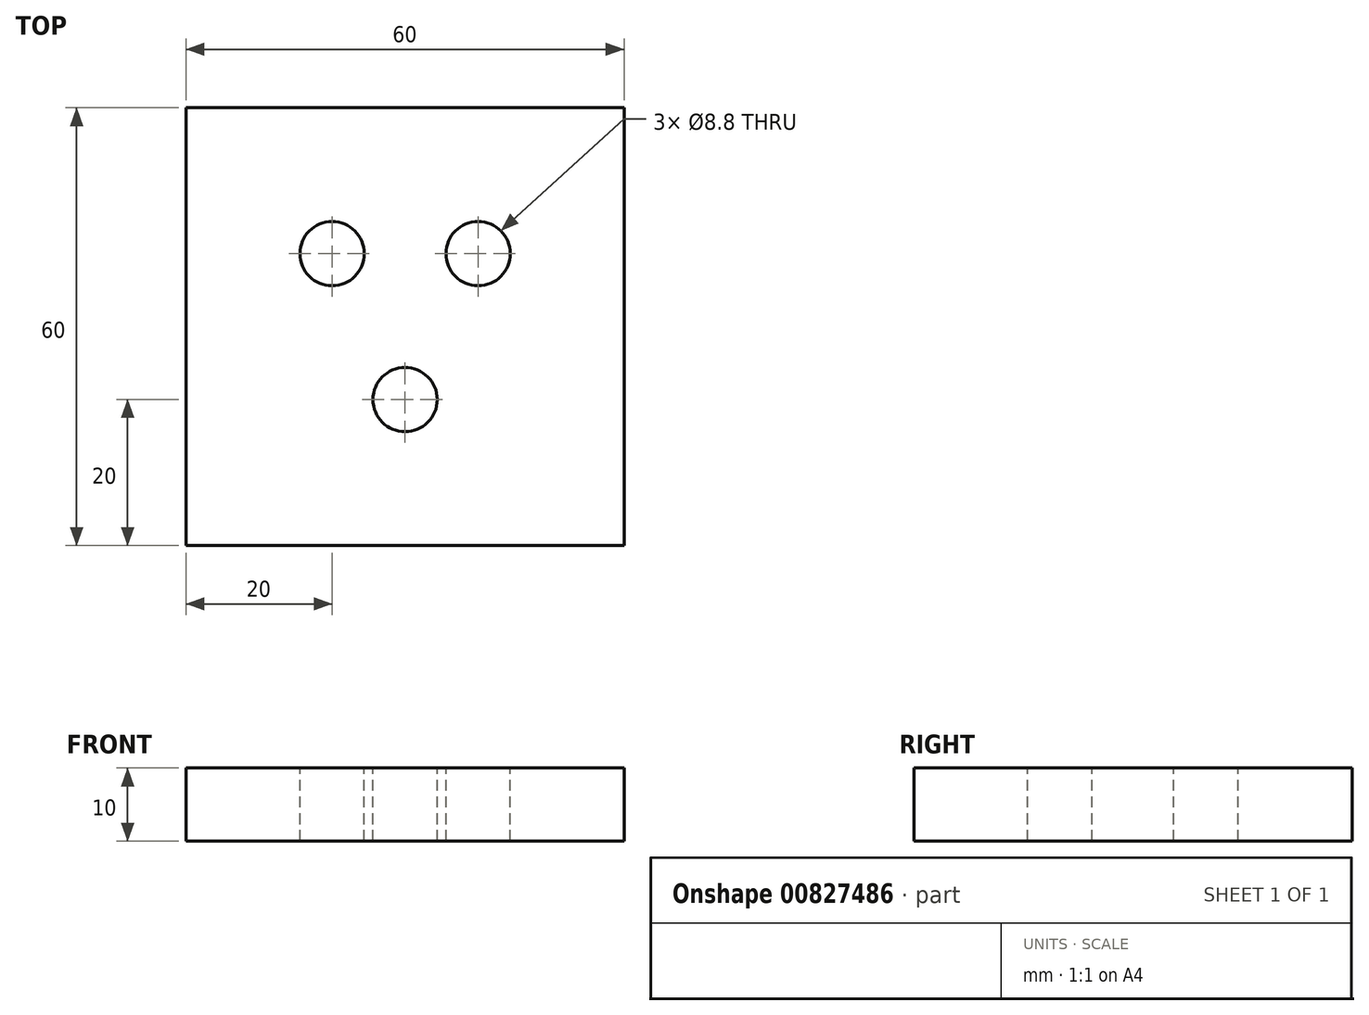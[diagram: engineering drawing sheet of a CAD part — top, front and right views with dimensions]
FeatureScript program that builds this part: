
annotation { "Feature Type Name" : "Feature", "Feature Type Description" : "" }
export const myFeature = defineFeature(function(context is Context, id is Id, definition is map)
    precondition{}
    {
        {
            var Q0;
            Q0=qCreatedBy(makeId("Top.planeOp"),FACE);
            var sketch = newSketch(context, id + "F0", { "sketchPlane" : qUnion([Q0])});
            skLineSegment(sketch, "E0.bottom", {"start": v(0, 0) * mm, "end": v(60, 0) * mm});
            skLineSegment(sketch, "E0.top", {"start": v(0, 60) * mm, "end": v(60, 60) * mm});
            skLineSegment(sketch, "E0.left", {"start": v(0, 0) * mm, "end": v(0, 60) * mm});
            skLineSegment(sketch, "E0.right", {"start": v(60, 0) * mm, "end": v(60, 60) * mm});
            skSolve(sketch);
        }
        {
            var Q0;
            Q0=makeQuery(id+"F0.imprint","IMPRINT",FACE,{"disambiguationData":[TD([[makeQuery(id+"F0.imprint","IMPRINT",EDGE,{"derivedFrom":sQuery(id+"F0.wireOp",EDGE,"E0.bottom")}),1.0]])]});
            extrude(context, id + "F1", {"entities" : qUnion([Q0]), "depth" : 10 * mm, "offsetDistance" : 25 * mm});
        }
        {
            var Q0;
            Q0=makeQuery(id+"F1.opExtrude","CAP_FACE",FACE,{"disambiguationData":[OSD([sQuery(id+"F0.wireOp",EDGE,"E0.bottom"),sQuery(id+"F0.wireOp",EDGE,"E0.top"),sQuery(id+"F0.wireOp",EDGE,"E0.left"),sQuery(id+"F0.wireOp",EDGE,"E0.right")])],"isStart":false});
            var sketch = newSketch(context, id + "F2", { "sketchPlane" : qUnion([Q0])});
            skPoint(sketch, "E1", {"position": v(20, 40) * mm});
            skPoint(sketch, "E2", {"position": v(40, 40) * mm});
            skPoint(sketch, "E3", {"position": v(30, 20) * mm});
            skPoint(sketch, "E3.positionSnap0", {"position": v(30, 0) * mm});
            skSolve(sketch);
        }
        {
            var Q0;
            Q0=sQuery(id+"F2.wireOp",VERTEX,"E1");
            var Q1;
            Q1=sQuery(id+"F2.wireOp",VERTEX,"E2");
            var Q2;
            Q2=sQuery(id+"F2.wireOp",VERTEX,"E3");
            var Q3;
            Q3=makeQuery(id+"F1.opExtrude","SWEPT_BODY",BODY,{"disambiguationData":[OSD([sQuery(id+"F0.wireOp",EDGE,"E0.bottom"),sQuery(id+"F0.wireOp",EDGE,"E0.top"),sQuery(id+"F0.wireOp",EDGE,"E0.left"),sQuery(id+"F0.wireOp",EDGE,"E0.right")])]});
            hole(context, id + "F3", {"style" : HoleStyle.SIMPLE, "endStyle" : HoleEndStyle.THROUGH, "standardTappedOrClearance" : lookupTablePath({ "standard" : "ISO", "fit" : "Normal", "size" : "M8", "type" : "Clearance" }), "standardBlindInLast" : lookupTablePath({ "fit" : "Standard", "standard" : "ISO", "size" : "M8", "type" : "Clearance" }), "holeDiameter" : 8.8 * mm, "majorDiameter" : 5 * mm, "isTappedThrough" : true, "tappedDepth" : 12 * mm, "tapClearance" : 3, "locations" : qUnion([Q0, Q1, Q2]), "scope" : qUnion([Q3])});
        }
    });
